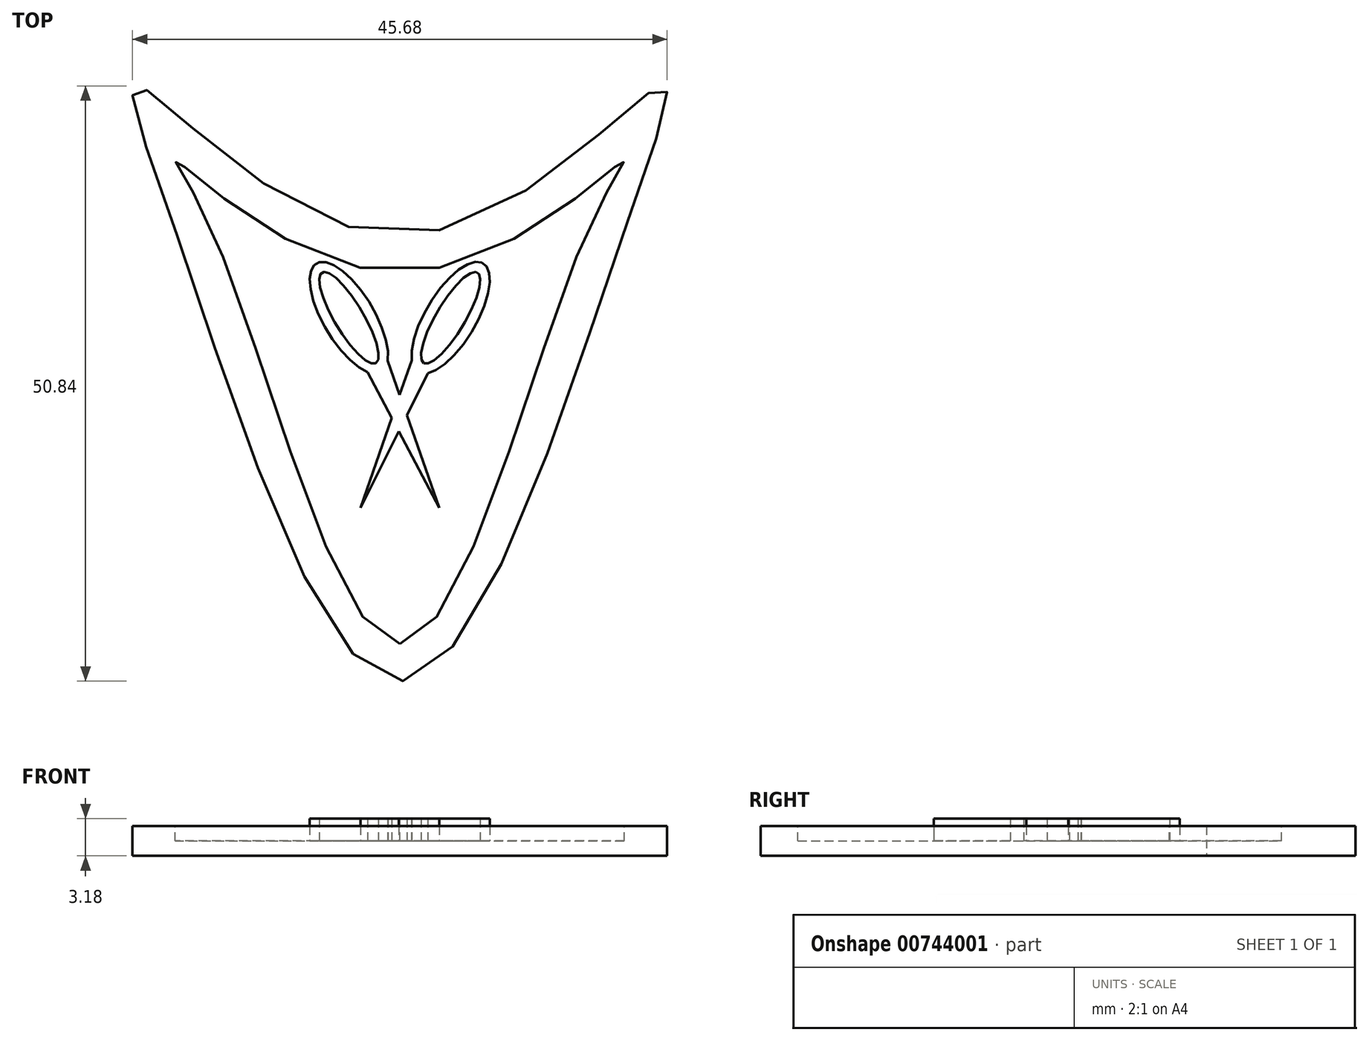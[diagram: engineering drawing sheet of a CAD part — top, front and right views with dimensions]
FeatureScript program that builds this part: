
annotation { "Feature Type Name" : "Feature", "Feature Type Description" : "" }
export const myFeature = defineFeature(function(context is Context, id is Id, definition is map)
    precondition{}
    {
        {
            var Q0;
            Q0=qCreatedBy(makeId("Top.planeOp"),FACE);
            var sketch = newSketch(context, id + "F0", { "sketchPlane" : qUnion([Q0])});
            skFitSpline(sketch, "E0", {"points": [v(-19.05, 0) * mm, v(0, -38.1) * mm, v(19.05, 0) * mm, v(22.23, 12.7) * mm, v(0, 0) * mm, v(-22.23, 12.7) * mm, v(-19.05, 0) * mm]});
            skSolve(sketch);
        }
        {
            var Q0;
            Q0=qSketchRegion(id+"F0",true);
            extrude(context, id + "F1", {"entities" : qUnion([Q0]), "depth" : 2.54 * mm, "offsetDistance" : 25.4 * mm});
        }
        {
            var Q0;
            Q0=makeQuery(id+"F1.opExtrude","CAP_FACE",FACE,{"disambiguationData":[OSD([sQuery(id+"F0.wireOp",EDGE,"E0")])],"isStart":false});
            var sketch = newSketch(context, id + "F2", { "sketchPlane" : qUnion([Q0])});
            skFitSpline(sketch, "E1", {"points": [v(0, -34.93) * mm, v(15.88, 0) * mm, v(19.05, 6.35) * mm, v(0, -3.18) * mm, v(-19.05, 6.35) * mm, v(-15.88, 0) * mm, v(0, -34.93) * mm]});
            skSolve(sketch);
        }
        {
            var Q0;
            Q0=qSketchRegion(id+"F2",true);
            extrude(context, id + "F3", {"entities" : qUnion([Q0]), "operationType" : NewBodyOperationType.REMOVE, "oppositeDirection" : true, "depth" : 1.27 * mm, "offsetDistance" : 25.4 * mm});
        }
        {
            var Q0;
            Q0=makeQuery(id+"F3.boolean.opBoolean","COPY",FACE,{"derivedFrom":makeQuery(id+"F3.opExtrude","CAP_FACE",FACE,{"disambiguationData":[OSD([sQuery(id+"F2.wireOp",EDGE,"E1")])],"isStart":false})});
            var sketch = newSketch(context, id + "F4", { "sketchPlane" : qUnion([Q0])});
            skLineSegment(sketch, "E2", {"start": v(-2.76, -11.7) * mm, "end": v(3.37, -23.3) * mm});
            skLineSegment(sketch, "E3", {"start": v(3.37, -23.3) * mm, "end": v(-1.02, -10.72) * mm});
            skEllipse(sketch, "E4", {"center": v(4.35, -7.06) * mm, "majorRadius": 5.42 * mm, "minorRadius": 2.17 * mm, "majorAxis": v(-0.51, -0.86)});
            skEllipse(sketch, "E5", {"center": v(4.35, -7.06) * mm, "majorRadius": 4.5 * mm, "minorRadius": 1.24 * mm, "majorAxis": v(-0.51, -0.86)});
            skLineSegment(sketch, "E6", {"start": v(-3.37, -23.3) * mm, "end": v(2.4, -11.81) * mm});
            skLineSegment(sketch, "E7", {"start": v(-3.37, -23.3) * mm, "end": v(1.02, -10.7) * mm});
            skEllipse(sketch, "E8.MirrorC", {"center": v(-4.35, -7.06) * mm, "majorRadius": 4.5 * mm, "minorRadius": 1.24 * mm, "majorAxis": v(0.51, -0.86)});
            skEllipse(sketch, "E9.MirrorC", {"center": v(-4.35, -7.06) * mm, "majorRadius": 5.42 * mm, "minorRadius": 2.17 * mm, "majorAxis": v(0.51, -0.86)});
            skSolve(sketch);
        }
        {
            var Q0;
            Q0=qSketchRegion(id+"F4",true);
            extrude(context, id + "F5", {"entities" : qUnion([Q0]), "operationType" : NewBodyOperationType.ADD, "depth" : 1.9 * mm, "offsetDistance" : 25.4 * mm});
        }
    });
